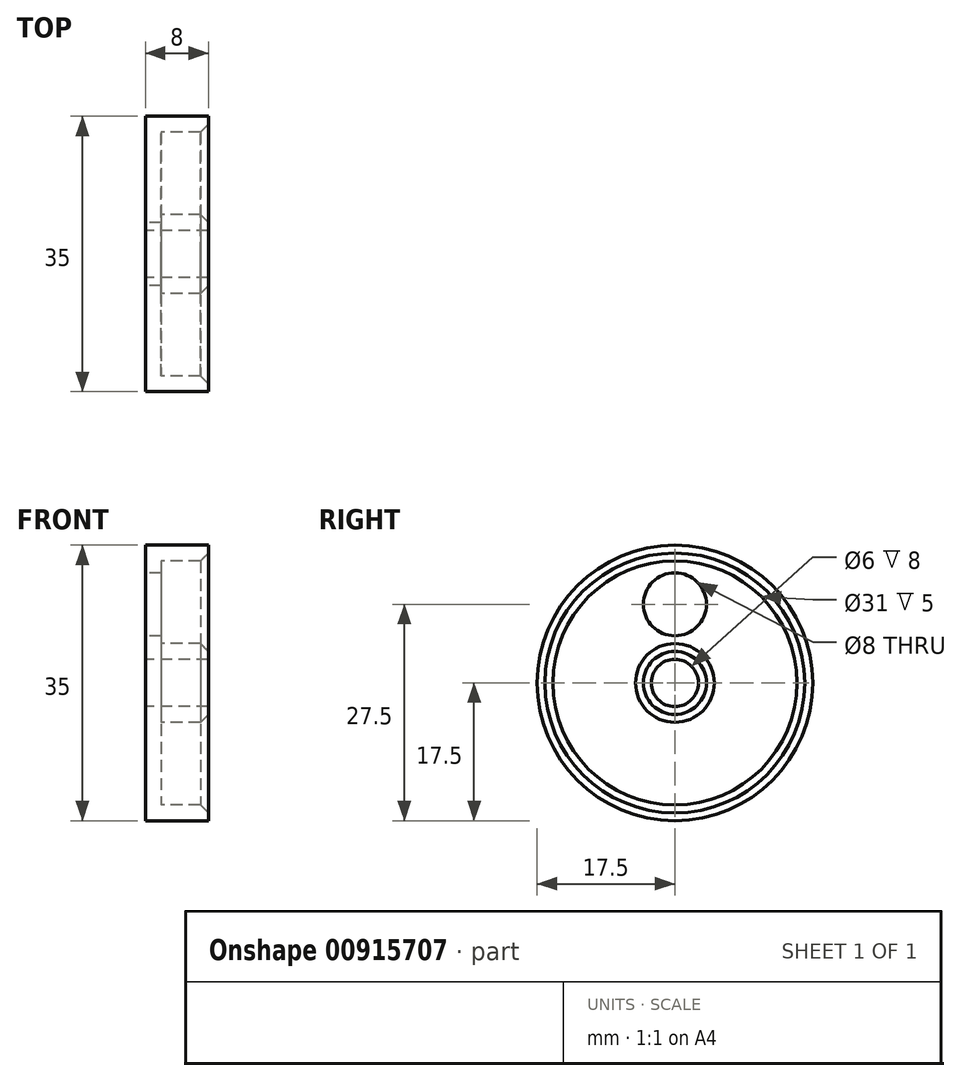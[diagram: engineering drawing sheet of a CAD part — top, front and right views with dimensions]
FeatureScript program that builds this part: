
annotation { "Feature Type Name" : "Feature", "Feature Type Description" : "" }
export const myFeature = defineFeature(function(context is Context, id is Id, definition is map)
    precondition{}
    {
        {
            var Q0;
            Q0=qCreatedBy(makeId("Top.planeOp"),FACE);
            var sketch = newSketch(context, id + "F0", { "sketchPlane" : qUnion([Q0])});
            skLineSegment(sketch, "E0.bottom", {"start": v(0, 0) * mm, "end": v(8, 0) * mm});
            skLineSegment(sketch, "E0.top", {"start": v(0, 17.5) * mm, "end": v(8, 17.5) * mm});
            skLineSegment(sketch, "E0.left", {"start": v(0, 0) * mm, "end": v(0, 17.5) * mm});
            skLineSegment(sketch, "E0.right", {"start": v(8, 0) * mm, "end": v(8, 17.5) * mm});
            skSolve(sketch);
        }
        {
            var Q0;
            Q0 = qSketchRegion(id + "F0", true);
            var Q1;
            Q1=sQuery(id+"F0.wireOp",EDGE,"E0.bottom");
            revolve(context, id + "F1", {"surfaceOperationType" : NewSurfaceOperationType.NEW, "entities" : qUnion([Q0]), "axis" : qUnion([Q1]), "revolveType" : RevolveType.FULL});
        }
        {
            var Q0;
            Q0=qCreatedBy(makeId("Right.planeOp"),FACE);
            var sketch = newSketch(context, id + "F2", { "sketchPlane" : qUnion([Q0])});
            skPoint(sketch, "E1", {"position": v(0, 0) * mm});
            skSolve(sketch);
        }
        {
            var Q0;
            Q0=sQuery(id+"F2.wireOp",VERTEX,"E1");
            var Q1;
            Q1=makeQuery(id+"F1.opRevolve","SWEPT_BODY",BODY,{"disambiguationData":[OSD([sQuery(id+"F0.wireOp",EDGE,"E0.bottom"),sQuery(id+"F0.wireOp",EDGE,"E0.top"),sQuery(id+"F0.wireOp",EDGE,"E0.left"),sQuery(id+"F0.wireOp",EDGE,"E0.right")])]});
            hole(context, id + "F3", {"style" : HoleStyle.SIMPLE, "endStyle" : HoleEndStyle.THROUGH, "oppositeDirection" : true, "holeDiameter" : 6 * mm, "majorDiameter" : 5 * mm, "isTappedThrough" : true, "tappedDepth" : 12 * mm, "tapClearance" : 3, "locations" : qUnion([Q0]), "scope" : qUnion([Q1])});
        }
        {
            var Q0;
            Q0=makeQuery(id+"F1.opRevolve","SWEPT_FACE",FACE,{"disambiguationData":[OSD([sQuery(id+"F0.wireOp",EDGE,"E0.right")])]});
            shell(context, id + "F4", {"entities" : qUnion([Q0]), "thickness" : 2 * mm});
        }
        {
            var Q0;
            Q0=makeQuery(id+"F1.opRevolve","SWEPT_FACE",FACE,{"disambiguationData":[OSD([sQuery(id+"F0.wireOp",EDGE,"E0.left")])]});
            var sketch = newSketch(context, id + "F5", { "sketchPlane" : qUnion([Q0])});
            skPoint(sketch, "E2", {"position": v(0, 10) * mm});
            skSolve(sketch);
        }
        {
            var Q0;
            Q0=sQuery(id+"F5.wireOp",VERTEX,"E2");
            var Q1;
            Q1=makeQuery(id+"F1.opRevolve","SWEPT_BODY",BODY,{"disambiguationData":[OSD([sQuery(id+"F0.wireOp",EDGE,"E0.bottom"),sQuery(id+"F0.wireOp",EDGE,"E0.top"),sQuery(id+"F0.wireOp",EDGE,"E0.left"),sQuery(id+"F0.wireOp",EDGE,"E0.right")])]});
            hole(context, id + "F6", {"style" : HoleStyle.SIMPLE, "endStyle" : HoleEndStyle.THROUGH, "holeDiameter" : 8 * mm, "majorDiameter" : 5 * mm, "isTappedThrough" : true, "tappedDepth" : 12 * mm, "tapClearance" : 3, "locations" : qUnion([Q0]), "scope" : qUnion([Q1])});
        }
        {
            var Q0;
            Q0=makeQuery(id+"F4.opShell","OFFSET_EDGE",EDGE,{"disambiguationData":[OSD([sQuery(id+"F0.wireOp",EDGE,"E0.right"),sQuery(id+"F3.hole-0.sketch.wireOp",EDGE,"core_line_2")])]});
            chamfer(context, id + "F7", {"entities" : qUnion([Q0]), "width" : 1 * mm, "tangentPropagation" : true});
        }
    });
